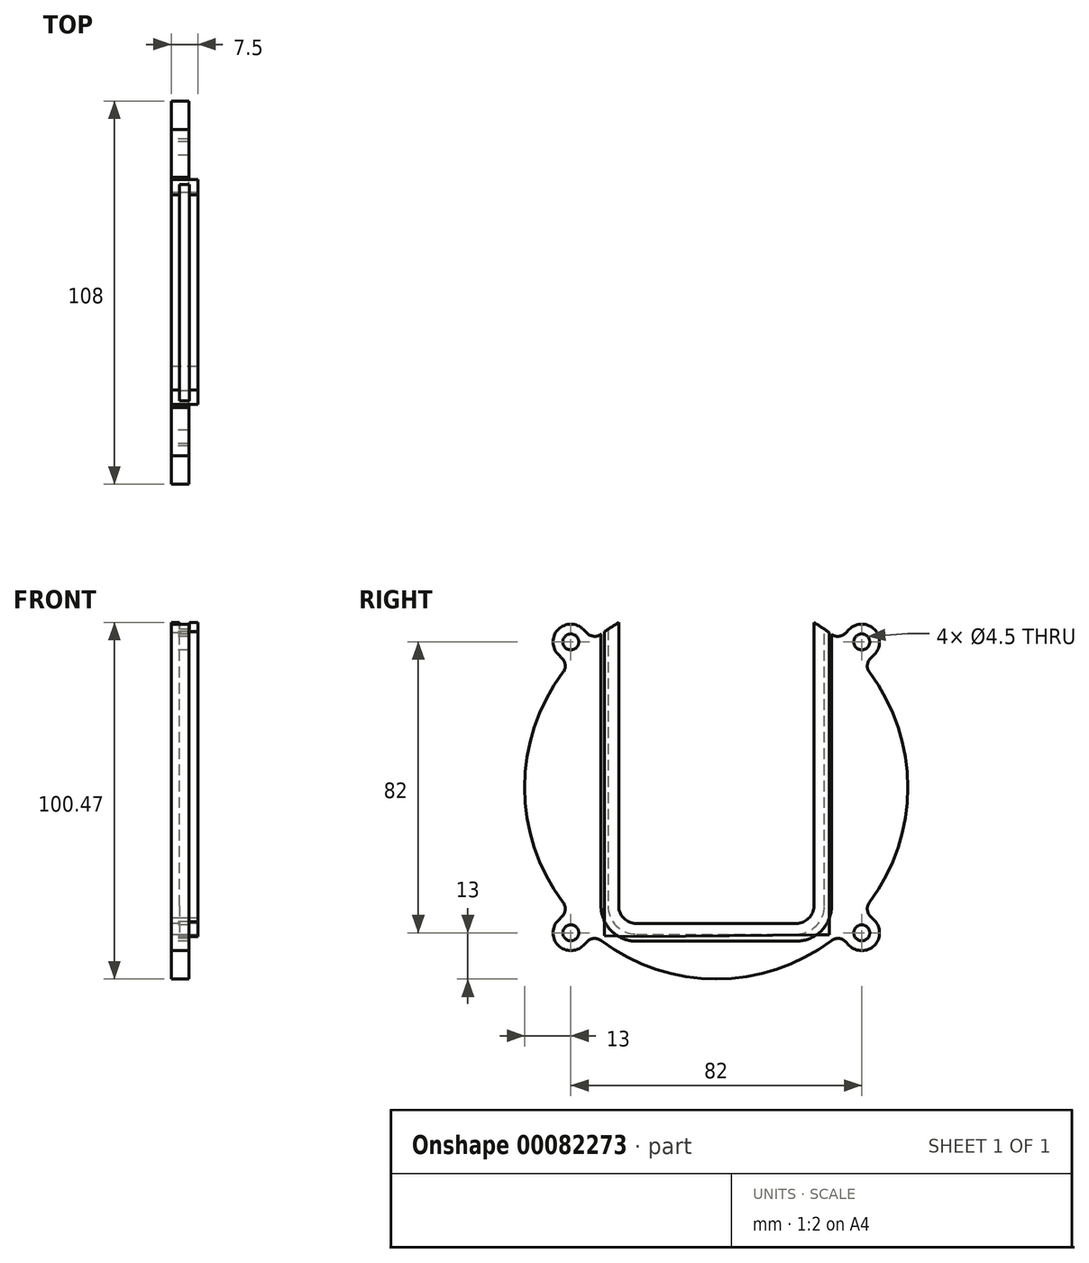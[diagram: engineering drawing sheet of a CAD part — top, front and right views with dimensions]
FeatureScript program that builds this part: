
annotation { "Feature Type Name" : "Feature", "Feature Type Description" : "" }
export const myFeature = defineFeature(function(context is Context, id is Id, definition is map)
    precondition{}
    {
        {
            var Q0;
            Q0=qCreatedBy(makeId("Right.planeOp"),FACE);
            var sketch = newSketch(context, id + "F0", { "sketchPlane" : qUnion([Q0])});
            skCircle(sketch, "E0", {"center": v(-41, 41) * mm, "radius": 2.25 * mm});
            skCircle(sketch, "E1", {"center": v(41, 41) * mm, "radius": 2.25 * mm});
            skCircle(sketch, "E2", {"center": v(41, -41) * mm, "radius": 2.25 * mm});
            skCircle(sketch, "E3", {"center": v(-41, -41) * mm, "radius": 2.25 * mm});
            skArc(sketch, "E4", {"start": v(-32.45, 43.16) * mm, "mid": v(-24.12, -48.31) * mm, "end": v(54, 0) * mm});
            skArc(sketch, "E5", {"start": v(37.46, -44.54) * mm, "mid": v(44.54, -44.54) * mm, "end": v(44.54, -37.46) * mm});
            skArc(sketch, "E6", {"start": v(-44.54, -37.46) * mm, "mid": v(-44.54, -44.54) * mm, "end": v(-37.46, -44.54) * mm});
            skLineSegment(sketch, "E7", {"start": v(-44.54, 37.46) * mm, "end": v(-36.42, 45.58) * mm, "construction": true});
            skLineSegment(sketch, "E8", {"start": v(-44.54, 37.46) * mm, "end": v(-43.44, 36.37) * mm});
            skLineSegment(sketch, "E9", {"start": v(-37.46, 44.54) * mm, "end": v(-36.37, 43.44) * mm});
            skLineSegment(sketch, "E10", {"start": v(37.46, 44.54) * mm, "end": v(46.12, 35.88) * mm, "construction": true});
            skLineSegment(sketch, "E11", {"start": v(37.46, 44.54) * mm, "end": v(36.37, 43.44) * mm});
            skLineSegment(sketch, "E12", {"start": v(44.54, 37.46) * mm, "end": v(43.44, 36.37) * mm});
            skLineSegment(sketch, "E13", {"start": v(-44.54, -37.46) * mm, "end": v(-35.54, -46.46) * mm, "construction": true});
            skLineSegment(sketch, "E14", {"start": v(-44.54, -37.46) * mm, "end": v(-43.44, -36.37) * mm});
            skLineSegment(sketch, "E15", {"start": v(-37.46, -44.54) * mm, "end": v(-36.37, -43.44) * mm});
            skLineSegment(sketch, "E16", {"start": v(37.46, -44.54) * mm, "end": v(47.36, -34.64) * mm, "construction": true});
            skLineSegment(sketch, "E17", {"start": v(37.46, -44.54) * mm, "end": v(36.37, -43.44) * mm});
            skLineSegment(sketch, "E18", {"start": v(44.54, -37.46) * mm, "end": v(43.44, -36.37) * mm});
            skArc(sketch, "E19.trimOffspring", {"start": v(-37.46, 44.54) * mm, "mid": v(-44.54, 44.54) * mm, "end": v(-44.54, 37.46) * mm});
            skArc(sketch, "E20.trimOffspring", {"start": v(32.45, 43.16) * mm, "mid": v(30.02, 44.89) * mm, "end": v(27.5, 46.47) * mm});
            skArc(sketch, "E21.trimOffspring", {"start": v(44.54, 37.46) * mm, "mid": v(44.54, 44.54) * mm, "end": v(37.46, 44.54) * mm});
            skArc(sketch, "E22.trimOffspring", {"start": v(-32.45, -43.16) * mm, "mid": v(0, -54) * mm, "end": v(32.45, -43.16) * mm});
            skPoint(sketch, "E23.visualSharp", {"position": v(-41.56, 34.48) * mm});
            skPoint(sketch, "E24.visualSharp", {"position": v(-34.48, 41.56) * mm});
            skArc(sketch, "E24.filletArc", {"start": v(-36.37, 43.44) * mm, "mid": v(-34.46, 42.57) * mm, "end": v(-32.45, 43.16) * mm});
            skPoint(sketch, "E25.visualSharp", {"position": v(-41.56, -34.48) * mm});
            skArc(sketch, "E25.filletArc", {"start": v(-43.44, -36.37) * mm, "mid": v(-42.57, -34.46) * mm, "end": v(-43.16, -32.45) * mm});
            skPoint(sketch, "E26.visualSharp", {"position": v(-34.48, -41.56) * mm});
            skArc(sketch, "E26.filletArc", {"start": v(-32.45, -43.16) * mm, "mid": v(-34.46, -42.57) * mm, "end": v(-36.37, -43.44) * mm});
            skPoint(sketch, "E27.visualSharp", {"position": v(41.56, -34.48) * mm});
            skArc(sketch, "E27.filletArc", {"start": v(43.16, -32.45) * mm, "mid": v(42.57, -34.46) * mm, "end": v(43.44, -36.37) * mm});
            skPoint(sketch, "E28.visualSharp", {"position": v(34.48, -41.56) * mm});
            skArc(sketch, "E28.filletArc", {"start": v(36.37, -43.44) * mm, "mid": v(34.46, -42.57) * mm, "end": v(32.45, -43.16) * mm});
            skPoint(sketch, "E29.visualSharp", {"position": v(41.56, 34.48) * mm});
            skArc(sketch, "E29.filletArc", {"start": v(43.44, 36.37) * mm, "mid": v(42.57, 34.46) * mm, "end": v(43.16, 32.45) * mm});
            skPoint(sketch, "E30.visualSharp", {"position": v(34.48, 41.56) * mm});
            skArc(sketch, "E30.filletArc", {"start": v(32.45, 43.16) * mm, "mid": v(34.46, 42.57) * mm, "end": v(36.37, 43.44) * mm});
            skArc(sketch, "E31.filletArc", {"start": v(-43.16, 32.45) * mm, "mid": v(-42.57, 34.46) * mm, "end": v(-43.44, 36.37) * mm});
            skArc(sketch, "E32.converted", {"start": v(-27.5, 46.47) * mm, "mid": v(0, -54) * mm, "end": v(27.5, 46.47) * mm});
            skLineSegment(sketch, "E33", {"start": v(-27.5, 46.47) * mm, "end": v(-27.5, -33.36) * mm});
            skLineSegment(sketch, "E34", {"start": v(27.5, 46.47) * mm, "end": v(27.5, -33.36) * mm});
            skCircle(sketch, "E35", {"center": v(0, 0) * mm, "radius": 17.5 * mm, "construction": true});
            skCircle(sketch, "E36", {"center": v(20.15, 20.15) * mm, "radius": 2.25 * mm, "construction": true});
            skCircle(sketch, "E37", {"center": v(-20.15, -20.15) * mm, "radius": 2.25 * mm, "construction": true});
            skLineSegment(sketch, "E38.bottom", {"start": v(-26.5, 26.5) * mm, "end": v(26.5, 26.5) * mm, "construction": true});
            skLineSegment(sketch, "E38.top", {"start": v(-26.5, -26.5) * mm, "end": v(26.5, -26.5) * mm, "construction": true});
            skLineSegment(sketch, "E38.left", {"start": v(-26.5, 26.5) * mm, "end": v(-26.5, -26.5) * mm, "construction": true});
            skLineSegment(sketch, "E38.right", {"start": v(26.5, 26.5) * mm, "end": v(26.5, -26.5) * mm, "construction": true});
            skArc(sketch, "E39.trimOffspring", {"start": v(-21.68, -18.5) * mm, "mid": v(-20.15, -20.15) * mm, "end": v(-18.5, -21.68) * mm, "construction": true});
            skArc(sketch, "E40.trimOffspring", {"start": v(21.68, 18.5) * mm, "mid": v(20.15, 20.15) * mm, "end": v(18.5, 21.68) * mm, "construction": true});
            skLineSegment(sketch, "E41", {"start": v(-22.5, -38.36) * mm, "end": v(22.5, -38.36) * mm});
            skPoint(sketch, "E42.orphan", {"position": v(-27.5, -21.94) * mm});
            skPoint(sketch, "E43.orphan", {"position": v(27.5, -21.94) * mm});
            skPoint(sketch, "E44.visualSharp", {"position": v(-27.5, -38.36) * mm});
            skArc(sketch, "E44.filletArc", {"start": v(-27.5, -33.36) * mm, "mid": v(-26.04, -36.9) * mm, "end": v(-22.5, -38.36) * mm});
            skPoint(sketch, "E45.visualSharp", {"position": v(27.5, -38.36) * mm});
            skArc(sketch, "E45.filletArc", {"start": v(22.5, -38.36) * mm, "mid": v(26.04, -36.9) * mm, "end": v(27.5, -33.36) * mm});
            skArc(sketch, "E46.trimOffspring", {"start": v(-27.5, 46.47) * mm, "mid": v(-30.02, 44.89) * mm, "end": v(-32.45, 43.16) * mm});
            skPoint(sketch, "E47.orphan", {"position": v(-27.5, 53.27) * mm});
            skPoint(sketch, "E48.orphan", {"position": v(27.5, 53.27) * mm});
            skLineSegment(sketch, "E49", {"start": v(-32.5, 43.12) * mm, "end": v(-32.5, -33.36) * mm});
            skLineSegment(sketch, "E50", {"start": v(-22.5, -43.36) * mm, "end": v(22.5, -43.36) * mm});
            skLineSegment(sketch, "E51", {"start": v(32.5, -33.36) * mm, "end": v(32.5, 43.12) * mm});
            skPoint(sketch, "E52.visualSharp", {"position": v(-32.5, -43.36) * mm});
            skArc(sketch, "E52.filletArc", {"start": v(-32.5, -33.36) * mm, "mid": v(-29.57, -40.43) * mm, "end": v(-22.5, -43.36) * mm});
            skPoint(sketch, "E53.visualSharp", {"position": v(32.5, -43.36) * mm});
            skArc(sketch, "E53.filletArc", {"start": v(22.5, -43.36) * mm, "mid": v(29.57, -40.43) * mm, "end": v(32.5, -33.36) * mm});
            skLineSegment(sketch, "E54", {"start": v(-31.46, 50.74) * mm, "end": v(-31.46, -33.36) * mm});
            skLineSegment(sketch, "E55", {"start": v(31.9, 48) * mm, "end": v(31.9, -33.36) * mm});
            skLineSegment(sketch, "E56", {"start": v(-20.83, -42.1) * mm, "end": v(31.9, -41.56) * mm});
            skLineSegment(sketch, "E57", {"start": v(31.9, -41.56) * mm, "end": v(31.9, -33.36) * mm});
            skLineSegment(sketch, "E58", {"start": v(-20.83, -42.1) * mm, "end": v(-31.46, -41.78) * mm});
            skLineSegment(sketch, "E59", {"start": v(-31.46, -41.78) * mm, "end": v(-31.46, -33.36) * mm});
            skSolve(sketch);
        }
        {
            var Q0;
            {var subQ4=sQuery(id+"F0.wireOp",EDGE,"E49");Q0=makeQuery(id+"F0.imprint","IMPRINT",FACE,{"disambiguationData":[TD([[makeQuery(id+"F0.imprint","IMPRINT",EDGE,{"derivedFrom":subQ4}),-1.0]])]});}
            var Q1;
            Q1=makeQuery(id+"F0.imprint","IMPRINT",FACE,{"disambiguationData":[TD([[makeQuery(id+"F0.imprint","IMPRINT",EDGE,{"derivedFrom":sQuery(id+"F0.wireOp",EDGE,"E0")}),-1.0]])]});
            var Q2;
            Q2=makeQuery(id+"F0.imprint","IMPRINT",FACE,{"disambiguationData":[TD([[makeQuery(id+"F0.imprint","IMPRINT",EDGE,{"derivedFrom":sQuery(id+"F0.wireOp",EDGE,"E1")}),-1.0]])]});
            var Q3;
            Q3=makeQuery(id+"F0.imprint","IMPRINT",FACE,{"disambiguationData":[TD([[makeQuery(id+"F0.imprint","IMPRINT",EDGE,{"derivedFrom":sQuery(id+"F0.wireOp",EDGE,"E2")}),-1.0]])]});
            var Q4;
            Q4=makeQuery(id+"F0.imprint","IMPRINT",FACE,{"disambiguationData":[TD([[makeQuery(id+"F0.imprint","IMPRINT",EDGE,{"derivedFrom":sQuery(id+"F0.wireOp",EDGE,"E3")}),-1.0]])]});
            extrude(context, id + "F1", {"entities" : qUnion([Q0, Q1, Q2, Q3, Q4]), "depth" : 5 * mm, "offsetDistance" : 25 * mm});
        }
        {
            var Q0;
            Q0=makeQuery(id+"F0.imprint","IMPRINT",FACE,{"disambiguationData":[TD([[makeQuery(id+"F0.imprint","IMPRINT",EDGE,{"derivedFrom":sQuery(id+"F0.wireOp",EDGE,"E33")}),-1.0]])]});
            extrude(context, id + "F2", {"entities" : qUnion([Q0]), "operationType" : NewBodyOperationType.ADD, "depth" : 7.5 * mm, "offsetDistance" : 25 * mm});
        }
        {
            var Q0;
            Q0=qCreatedBy(makeId("Top.planeOp"),FACE);
            var Q1;
            Q1=sQuery(id+"F0.wireOp",VERTEX,"E32.converted.start");
            cPlane(context, id + "F3", {"entities" : qUnion([Q0, Q1]), "cplaneType" : CPlaneType.PLANE_POINT, "offset" : 30.6 * mm, "width" : 150 * mm, "height" : 150 * mm});
        }
        {
            var Q0;
            Q0=qCreatedBy(id+"F3.planeOp",FACE);
            var sketch = newSketch(context, id + "F4", { "sketchPlane" : qUnion([Q0])});
            skLineSegment(sketch, "E60.bottom", {"start": v(2.38, -30.5) * mm, "end": v(5.12, -30.5) * mm});
            skLineSegment(sketch, "E60.top", {"start": v(2.37, -25.5) * mm, "end": v(5.12, -25.5) * mm});
            skLineSegment(sketch, "E60.left", {"start": v(2.38, -30.5) * mm, "end": v(2.37, -25.5) * mm});
            skLineSegment(sketch, "E60.right", {"start": v(5.12, -30.5) * mm, "end": v(5.12, -25.5) * mm});
            skSolve(sketch);
        }
        {
            var Q0;
            Q0=makeQuery(id+"F4.imprint","IMPRINT",FACE,{"disambiguationData":[TD([[makeQuery(id+"F4.imprint","IMPRINT",EDGE,{"derivedFrom":sQuery(id+"F4.wireOp",EDGE,"E60.bottom")}),1.0]])]});
            var Q1;
            Q1=sQuery(id+"F0.wireOp",EDGE,"E33");
            var Q2;
            Q2=sQuery(id+"F0.wireOp",EDGE,"E44.filletArc");
            var Q3;
            Q3=sQuery(id+"F0.wireOp",EDGE,"E41");
            var Q4;
            Q4=sQuery(id+"F0.wireOp",EDGE,"E45.filletArc");
            var Q5;
            Q5=sQuery(id+"F0.wireOp",EDGE,"E34");
            sweep(context, id + "F5", {"operationType" : NewBodyOperationType.REMOVE, "profiles" : qUnion([Q0]), "path" : qUnion([Q1, Q2, Q3, Q4, Q5])});
        }
    });
